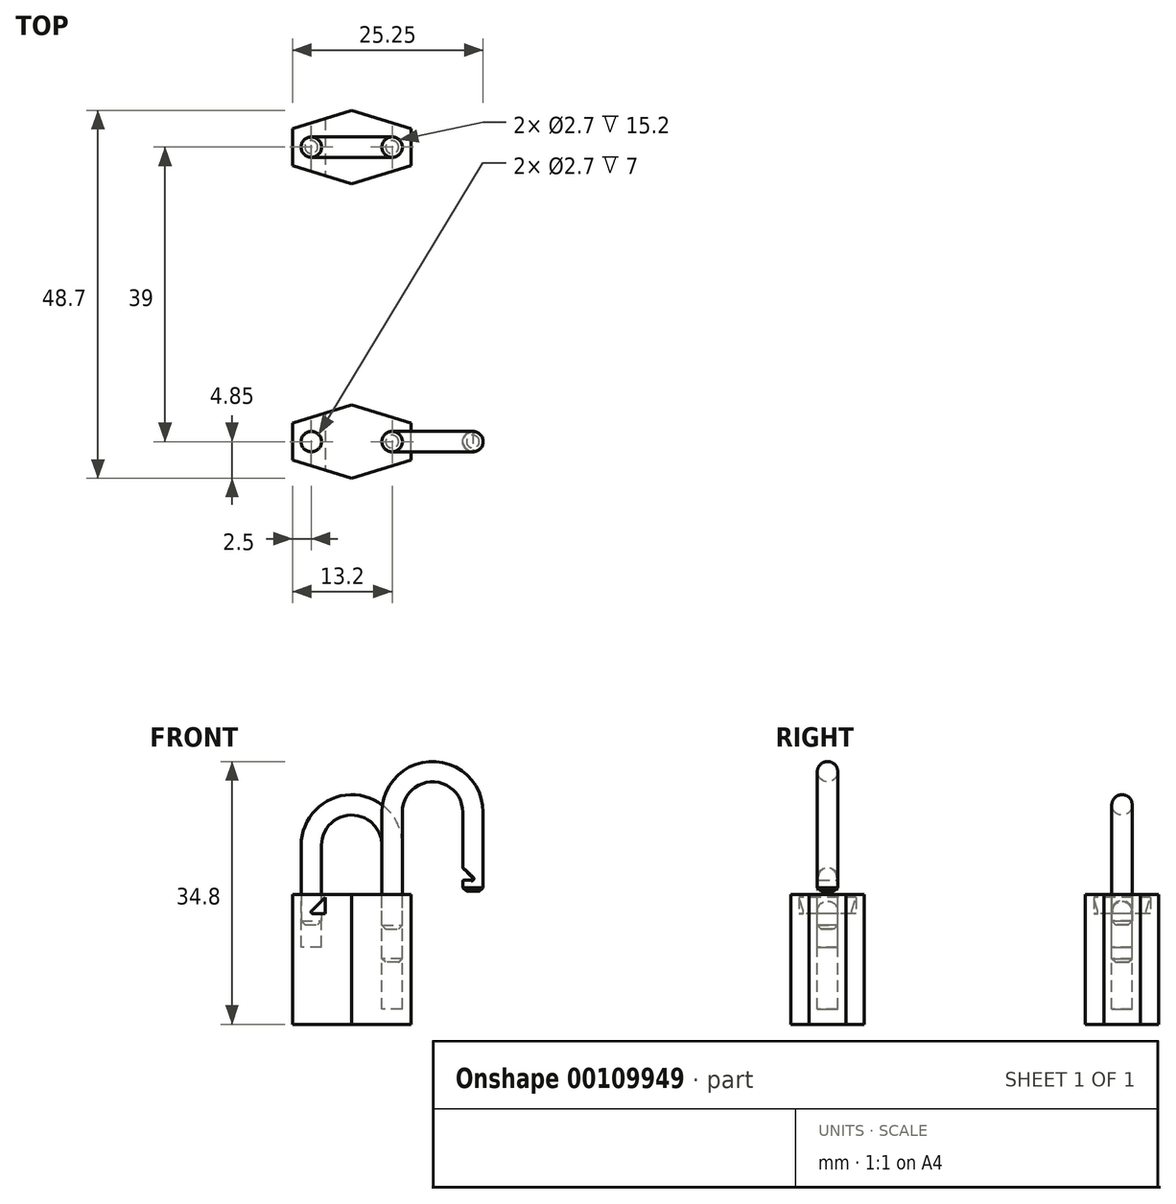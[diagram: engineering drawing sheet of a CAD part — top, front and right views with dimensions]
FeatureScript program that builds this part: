
annotation { "Feature Type Name" : "Feature", "Feature Type Description" : "" }
export const myFeature = defineFeature(function(context is Context, id is Id, definition is map)
    precondition{}
    {
        {
            assignVariable(context, id + "F0", {"name" : "Body_Depth", "anyValue" : 9.7});
        }
        {
            assignVariable(context, id + "F1", {"name" : "Body_Height", "anyValue" : 17.2});
        }
        {
            var Q0;
            Q0=qCreatedBy(makeId("Front.planeOp"),FACE);
            var sketch = newSketch(context, id + "F2", { "sketchPlane" : qUnion([Q0])});
            skLineSegment(sketch, "E0.bottom", {"start": v(-7.85, 0) * mm, "end": v(7.85, 0) * mm});
            skLineSegment(sketch, "E0.top", {"start": v(-7.85, -17.2) * mm, "end": v(7.85, -17.2) * mm});
            skLineSegment(sketch, "E0.left", {"start": v(-7.85, 0) * mm, "end": v(-7.85, -17.2) * mm});
            skLineSegment(sketch, "E0.right", {"start": v(7.85, 0) * mm, "end": v(7.85, -17.2) * mm});
            skSolve(sketch);
        }
        {
            var Q0;
            Q0=qSketchRegion(id+"F2",true);
            extrude(context, id + "F3", {"entities" : qUnion([Q0]), "endBound" : BoundingType.SYMMETRIC, "depth" : (getVariable(context, 'Body_Depth')) * mm});
        }
        {
            var Q0;
            Q0=makeQuery(id+"F3.opExtrude","SWEPT_FACE",FACE,{"disambiguationData":[OSD([sQuery(id+"F2.wireOp",EDGE,"E0.bottom")])]});
            var sketch = newSketch(context, id + "F4", { "sketchPlane" : qUnion([Q0])});
            skLineSegment(sketch, "E1", {"start": v(0, -4.85) * mm, "end": v(-7.85, -2.42) * mm});
            skLineSegment(sketch, "E2", {"start": v(-7.85, -2.42) * mm, "end": v(-7.85, -4.85) * mm});
            skLineSegment(sketch, "E3", {"start": v(-7.85, -4.85) * mm, "end": v(0, -4.85) * mm});
            skLineSegment(sketch, "E4", {"start": v(-10.8, 0) * mm, "end": v(12.74, 0) * mm, "construction": true});
            skLineSegment(sketch, "E5", {"start": v(0, -10) * mm, "end": v(0, 11.03) * mm, "construction": true});
            skPoint(sketch, "E5.endSnap0", {"position": v(0, 4.85) * mm});
            skLineSegment(sketch, "E6.MirrorCS", {"start": v(0, 4.85) * mm, "end": v(-7.85, 2.42) * mm});
            skLineSegment(sketch, "E7.MirrorCS", {"start": v(-7.85, 2.42) * mm, "end": v(-7.85, 4.85) * mm});
            skLineSegment(sketch, "E8.MirrorCS", {"start": v(-7.85, 4.85) * mm, "end": v(0, 4.85) * mm});
            skLineSegment(sketch, "E9.MirrorCS", {"start": v(7.85, 4.85) * mm, "end": v(0, 4.85) * mm});
            skLineSegment(sketch, "E10.MirrorCS", {"start": v(7.85, 2.42) * mm, "end": v(7.85, 4.85) * mm});
            skLineSegment(sketch, "E11.MirrorCS", {"start": v(0, 4.85) * mm, "end": v(7.85, 2.42) * mm});
            skLineSegment(sketch, "E12.MirrorCS", {"start": v(7.85, -4.85) * mm, "end": v(0, -4.85) * mm});
            skLineSegment(sketch, "E13.MirrorCS", {"start": v(7.85, -2.42) * mm, "end": v(7.85, -4.85) * mm});
            skLineSegment(sketch, "E14.MirrorCS", {"start": v(0, -4.85) * mm, "end": v(7.85, -2.42) * mm});
            skSolve(sketch);
        }
        {
            var Q0;
            Q0=qSketchRegion(id+"F4",true);
            extrude(context, id + "F5", {"entities" : qUnion([Q0]), "operationType" : NewBodyOperationType.REMOVE, "endBound" : BoundingType.THROUGH_ALL, "oppositeDirection" : true, "depth" : 25 * mm});
        }
        {
            var Q0;
            Q0=makeQuery(id+"F3.opExtrude","SWEPT_FACE",FACE,{"disambiguationData":[OSD([sQuery(id+"F2.wireOp",EDGE,"E0.bottom")])]});
            var sketch = newSketch(context, id + "F6", { "sketchPlane" : qUnion([Q0])});
            skLineSegment(sketch, "E15", {"start": v(-7.85, 0) * mm, "end": v(7.85, 0) * mm, "construction": true});
            skLineSegment(sketch, "E16", {"start": v(0, 4.85) * mm, "end": v(0, -4.85) * mm, "construction": true});
            skCircle(sketch, "E17", {"center": v(5.35, 0) * mm, "radius": 1.35 * mm});
            skCircle(sketch, "E18", {"center": v(-5.35, 0) * mm, "radius": 1.35 * mm});
            skPoint(sketch, "E19", {"position": v(0, -4.85) * mm});
            skPoint(sketch, "E20", {"position": v(0, 4.85) * mm});
            skPoint(sketch, "E21", {"position": v(7.85, 0) * mm});
            skPoint(sketch, "E22", {"position": v(-7.85, 0) * mm});
            skSolve(sketch);
        }
        {
            var Q0;
            Q0=makeQuery(id+"F6.imprint","IMPRINT",FACE,{"disambiguationData":[TD([[makeQuery(id+"F6.imprint","IMPRINT",EDGE,{"derivedFrom":sQuery(id+"F6.wireOp",EDGE,"E17")}),1.0]])]});
            extrude(context, id + "F7", {"entities" : qUnion([Q0]), "operationType" : NewBodyOperationType.REMOVE, "oppositeDirection" : true, "depth" : (getVariable(context, 'Body_Height') - 2) * mm});
        }
        {
            var Q0;
            Q0=makeQuery(id+"F6.imprint","IMPRINT",FACE,{"disambiguationData":[TD([[makeQuery(id+"F6.imprint","IMPRINT",EDGE,{"derivedFrom":sQuery(id+"F6.wireOp",EDGE,"E18")}),1.0]])]});
            extrude(context, id + "F8", {"entities" : qUnion([Q0]), "operationType" : NewBodyOperationType.REMOVE, "oppositeDirection" : true, "depth" : 7 * mm});
        }
        {
            var Q0;
            Q0=qCreatedBy(makeId("Front.planeOp"),FACE);
            var sketch = newSketch(context, id + "F9", { "sketchPlane" : qUnion([Q0])});
            skPoint(sketch, "E23.0", {"position": v(5.35, 0) * mm});
            skPoint(sketch, "E24.0", {"position": v(-5.35, 0) * mm});
            skLineSegment(sketch, "E25.0", {"start": v(-7.85, 0) * mm, "end": v(7.85, 0) * mm, "construction": true});
            skLineSegment(sketch, "E26", {"start": v(5.35, -9) * mm, "end": v(5.35, 6.5) * mm});
            skArc(sketch, "E27", {"start": v(5.35, 6.5) * mm, "mid": v(0, 11.85) * mm, "end": v(-5.35, 6.5) * mm});
            skLineSegment(sketch, "E28", {"start": v(0, 12.3) * mm, "end": v(0, -9.7) * mm, "construction": true});
            skPoint(sketch, "E29", {"position": v(0, 11.85) * mm});
            skLineSegment(sketch, "E30", {"start": v(-5.35, 6.5) * mm, "end": v(-5.35, -4) * mm});
            skSolve(sketch);
        }
        {
            var Q0;
            Q0=sQuery(id+"F9.wireOp",VERTEX,"E26.start");
            var Q1;
            Q1=sQuery(id+"F9.wireOp",EDGE,"E26");
            cPlane(context, id + "F10", {"entities" : qUnion([Q0, Q1]), "cplaneType" : CPlaneType.LINE_POINT, "offset" : 25 * mm, "width" : 150 * mm, "height" : 150 * mm});
        }
        {
            var Q0;
            Q0=qCreatedBy(id+"F10.planeOp",FACE);
            var sketch = newSketch(context, id + "F11", { "sketchPlane" : qUnion([Q0])});
            skCircle(sketch, "E31.0", {"center": v(5.35, 0) * mm, "radius": 1.35 * mm});
            skSolve(sketch);
        }
        {
            var Q0;
            Q0=makeQuery(id+"F11.imprint","IMPRINT",FACE,{"disambiguationData":[TD([[makeQuery(id+"F11.imprint","IMPRINT",EDGE,{"derivedFrom":sQuery(id+"F11.wireOp",EDGE,"E31.0")}),1.0]])]});
            var Q1;
            Q1=qConstructionFilter(qBodyType(qCreatedBy(id+"F9",EDGE),BodyType.WIRE),ConstructionObject.NO);
            sweep(context, id + "F12", {"profiles" : qUnion([Q0]), "path" : qUnion([Q1])});
        }
        {
            var Q0;
            Q0=makeQuery(id+"F12.opSweep","CAP_FACE",FACE,{"disambiguationData":[OSD([sQuery(id+"F9.wireOp",VERTEX,"E26.start"),sQuery(id+"F11.wireOp",EDGE,"E31.0")])],"isStart":true});
            var Q1;
            Q1=makeQuery(id+"F12.opSweep","CAP_FACE",FACE,{"disambiguationData":[OSD([sQuery(id+"F9.wireOp",VERTEX,"E30.end"),sQuery(id+"F11.wireOp",EDGE,"E31.0")])],"isStart":false});
            chamfer(context, id + "F13", {"entities" : qUnion([Q0, Q1]), "width" : .5 * mm, "tangentPropagation" : true});
        }
        {
            var Q0;
            Q0=qCreatedBy(makeId("Front.planeOp"),FACE);
            var sketch = newSketch(context, id + "F14", { "sketchPlane" : qUnion([Q0])});
            skLineSegment(sketch, "E32", {"start": v(-3.53, -0.43) * mm, "end": v(-5.64, -2.53) * mm});
            skLineSegment(sketch, "E33", {"start": v(-5.64, -2.53) * mm, "end": v(-3.53, -2.53) * mm});
            skLineSegment(sketch, "E34", {"start": v(-3.53, -2.53) * mm, "end": v(-3.53, -0.43) * mm});
            skSolve(sketch);
        }
        {
            var Q0;
            Q0=qSketchRegion(id+"F14",true);
            extrude(context, id + "F15", {"entities" : qUnion([Q0]), "operationType" : NewBodyOperationType.REMOVE, "endBound" : BoundingType.SYMMETRIC, "oppositeDirection" : true, "depth" : 25 * mm});
        }
        {
            var Q0;
            Q0=makeQuery(id+"F15.boolean.opBoolean","COPY",EDGE,{"derivedFrom":makeQuery(id+"F15.opExtrude","SWEPT_EDGE",EDGE,{"disambiguationData":[OSD([sQuery(id+"F14.wireOp",EDGE,"E32"),sQuery(id+"F14.wireOp",EDGE,"E33")])]})});
            fillet(context, id + "F16", {"entities" : qUnion([Q0]), "radius" : .2 * mm, "tangentPropagation" : true, "allowEdgeOverflow" : false});
        }
        {
            var Q0;
            Q0=makeQuery(id+"F15.boolean.opBoolean","INTERSECT",EDGE,{"derivedFrom":[makeQuery(id+"F12.opSweep","SWEPT_FACE",FACE,{"disambiguationData":[OSD([sQuery(id+"F9.wireOp",EDGE,"E30"),sQuery(id+"F11.wireOp",EDGE,"E31.0")])]}),makeQuery(id+"F15.opExtrude","SWEPT_FACE",FACE,{"disambiguationData":[OSD([sQuery(id+"F14.wireOp",EDGE,"E33")])]})]});
            fillet(context, id + "F17", {"entities" : qUnion([Q0]), "radius" : .1 * mm, "tangentPropagation" : true, "allowEdgeOverflow" : false});
        }
        {
            var Q0;
            Q0=makeQuery(id+"F3.opExtrude","SWEPT_BODY",BODY,{"disambiguationData":[OSD([sQuery(id+"F2.wireOp",EDGE,"E0.bottom"),sQuery(id+"F2.wireOp",EDGE,"E0.top"),sQuery(id+"F2.wireOp",EDGE,"E0.left"),sQuery(id+"F2.wireOp",EDGE,"E0.right")])]});
            var Q1;
            Q1=makeQuery(id+"F12.opSweep","SWEPT_BODY",BODY,{"disambiguationData":[OSD([sQuery(id+"F9.wireOp",EDGE,"E30"),sQuery(id+"F11.wireOp",EDGE,"E31.0")])]});
            transform(context, id + "F18", {"entities" : qUnion([Q0, Q1]), "transformType" : TransformType.COPY});
        }
        {
            var Q0;
            Q0=makeQuery(id+"F18.opPattern","COPY",BODY,{"derivedFrom":makeQuery(id+"F3.opExtrude","SWEPT_BODY",BODY,{"disambiguationData":[OSD([sQuery(id+"F2.wireOp",EDGE,"E0.bottom"),sQuery(id+"F2.wireOp",EDGE,"E0.top"),sQuery(id+"F2.wireOp",EDGE,"E0.left"),sQuery(id+"F2.wireOp",EDGE,"E0.right")])]}),"instanceName":"1"});
            var Q1;
            Q1=makeQuery(id+"F18.opPattern","COPY",BODY,{"derivedFrom":makeQuery(id+"F12.opSweep","SWEPT_BODY",BODY,{"disambiguationData":[OSD([sQuery(id+"F9.wireOp",EDGE,"E30"),sQuery(id+"F11.wireOp",EDGE,"E31.0")])]}),"instanceName":"1"});
            transform(context, id + "F19", {"entities" : qUnion([Q0, Q1]), "transformType" : TransformType.TRANSLATION_3D, "dx" : 0 * mm, "dy" : -39 * mm, "dz" : 0 * mm, "makeCopy" : false});
        }
        {
            var Q0;
            Q0=makeQuery(id+"F18.opPattern","COPY",BODY,{"derivedFrom":makeQuery(id+"F12.opSweep","SWEPT_BODY",BODY,{"disambiguationData":[OSD([sQuery(id+"F9.wireOp",EDGE,"E30"),sQuery(id+"F11.wireOp",EDGE,"E31.0")])]}),"instanceName":"1"});
            var Q1;
            Q1=sQuery(id+"F9.wireOp",EDGE,"E26");
            transform(context, id + "F20", {"entities" : qUnion([Q0]), "transformType" : TransformType.TRANSLATION_DISTANCE, "transformDirection" : qUnion([Q1]), "distance" : 4.4 * mm, "makeCopy" : false});
        }
        {
            var Q0;
            Q0=makeQuery(id+"F18.opPattern","COPY",BODY,{"derivedFrom":makeQuery(id+"F12.opSweep","SWEPT_BODY",BODY,{"disambiguationData":[OSD([sQuery(id+"F9.wireOp",EDGE,"E30"),sQuery(id+"F11.wireOp",EDGE,"E31.0")])]}),"instanceName":"1"});
            var Q1;
            Q1=makeQuery(id+"F18.opPattern","COPY",FACE,{"derivedFrom":makeQuery(id+"F12.opSweep","SWEPT_FACE",FACE,{"disambiguationData":[OSD([sQuery(id+"F9.wireOp",EDGE,"E26"),sQuery(id+"F11.wireOp",EDGE,"E31.0")])]}),"instanceName":"1"});
            transform(context, id + "F21", {"entities" : qUnion([Q0]), "transformType" : TransformType.ROTATION, "transformAxis" : qUnion([Q1]), "angle" : 180 * degree, "makeCopy" : false});
        }
    });
